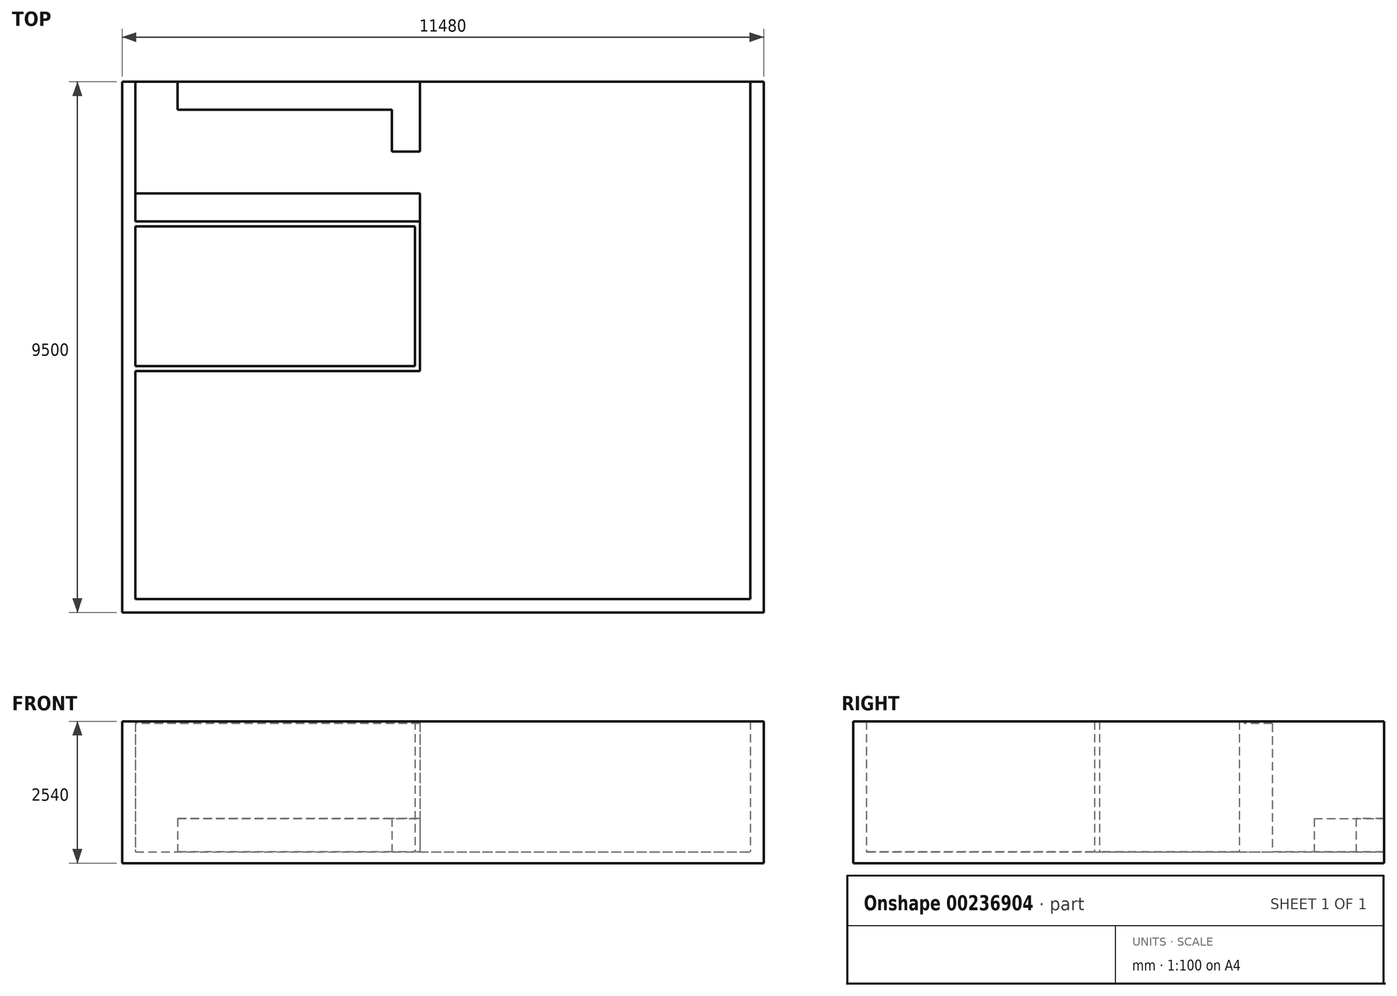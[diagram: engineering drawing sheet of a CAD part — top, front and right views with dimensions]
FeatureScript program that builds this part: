
annotation { "Feature Type Name" : "Feature", "Feature Type Description" : "" }
export const myFeature = defineFeature(function(context is Context, id is Id, definition is map)
    precondition{}
    {
        {
            var Q0;
            Q0=qCreatedBy(makeId("Top.planeOp"),FACE);
            var sketch = newSketch(context, id + "F0", { "sketchPlane" : qUnion([Q0])});
            skLineSegment(sketch, "E0.bottom", {"start": v(-5740, -4750) * mm, "end": v(5740, -4750) * mm});
            skLineSegment(sketch, "E0.top", {"start": v(-5740, 4750) * mm, "end": v(5740, 4750) * mm});
            skLineSegment(sketch, "E0.left", {"start": v(-5740, -4750) * mm, "end": v(-5740, 4750) * mm});
            skLineSegment(sketch, "E0.right", {"start": v(5740, -4750) * mm, "end": v(5740, 4750) * mm});
            skSolve(sketch);
        }
        {
            var Q0;
            Q0=makeQuery(id+"F0.imprint","IMPRINT",FACE,{"disambiguationData":[TD([[makeQuery(id+"F0.imprint","IMPRINT",EDGE,{"derivedFrom":sQuery(id+"F0.wireOp",EDGE,"E0.bottom")}),1.0]])]});
            extrude(context, id + "F1", {"entities" : qUnion([Q0]), "oppositeDirection" : true, "depth" : 200 * mm});
        }
        {
            var Q0;
            Q0=makeQuery(id+"F1.opExtrude","CAP_FACE",FACE,{"disambiguationData":[OSD([sQuery(id+"F0.wireOp",EDGE,"E0.bottom"),sQuery(id+"F0.wireOp",EDGE,"E0.top"),sQuery(id+"F0.wireOp",EDGE,"E0.left"),sQuery(id+"F0.wireOp",EDGE,"E0.right")])],"isStart":true});
            var sketch = newSketch(context, id + "F2", { "sketchPlane" : qUnion([Q0])});
            skLineSegment(sketch, "E1.bottom", {"start": v(-5740, 4750) * mm, "end": v(-5500, 4750) * mm});
            skLineSegment(sketch, "E1.top", {"start": v(-5740, -4750) * mm, "end": v(-5500, -4750) * mm});
            skLineSegment(sketch, "E1.left", {"start": v(-5740, 4750) * mm, "end": v(-5740, -4750) * mm});
            skLineSegment(sketch, "E1.right", {"start": v(-5500, 4750) * mm, "end": v(-5500, -4510) * mm});
            skLineSegment(sketch, "E2.bottom", {"start": v(-5500, -4750) * mm, "end": v(5740, -4750) * mm});
            skLineSegment(sketch, "E2.top", {"start": v(-5500, -4510) * mm, "end": v(5500, -4510) * mm});
            skLineSegment(sketch, "E2.right", {"start": v(5740, -4750) * mm, "end": v(5740, -4510) * mm});
            skLineSegment(sketch, "E3.top", {"start": v(5740, 4750) * mm, "end": v(5500, 4750) * mm});
            skLineSegment(sketch, "E3.left", {"start": v(5740, -4510) * mm, "end": v(5740, 4750) * mm});
            skLineSegment(sketch, "E3.right", {"start": v(5500, -4510) * mm, "end": v(5500, 4750) * mm});
            skSolve(sketch);
        }
        {
            var Q0;
            Q0=makeQuery(id+"F2.imprint","IMPRINT",FACE,{"disambiguationData":[TD([[makeQuery(id+"F2.imprint","IMPRINT",EDGE,{"derivedFrom":sQuery(id+"F2.wireOp",EDGE,"E1.bottom")}),-1.0]])]});
            extrude(context, id + "F3", {"entities" : qUnion([Q0]), "operationType" : NewBodyOperationType.ADD, "depth" : 2340 * mm});
        }
        {
            var Q0;
            Q0=makeQuery(id+"F1.opExtrude","CAP_FACE",FACE,{"disambiguationData":[OSD([sQuery(id+"F0.wireOp",EDGE,"E0.bottom"),sQuery(id+"F0.wireOp",EDGE,"E0.top"),sQuery(id+"F0.wireOp",EDGE,"E0.left"),sQuery(id+"F0.wireOp",EDGE,"E0.right")])],"isStart":true});
            var sketch = newSketch(context, id + "F4", { "sketchPlane" : qUnion([Q0])});
            skLineSegment(sketch, "E4.bottom", {"start": v(-5500, -430) * mm, "end": v(-410, -430) * mm});
            skLineSegment(sketch, "E4.top", {"start": v(-5500, -340) * mm, "end": v(-500, -340) * mm});
            skLineSegment(sketch, "E4.left", {"start": v(-5500, -430) * mm, "end": v(-5500, -340) * mm});
            skLineSegment(sketch, "E4.right", {"start": v(-410, -430) * mm, "end": v(-410, -340) * mm});
            skLineSegment(sketch, "E5.left", {"start": v(-410, 2160) * mm, "end": v(-410, 2160) * mm});
            skLineSegment(sketch, "E6.bottom", {"start": v(-500, 2160) * mm, "end": v(-5500, 2160) * mm});
            skLineSegment(sketch, "E6.top", {"start": v(-410, 2250) * mm, "end": v(-5500, 2250) * mm});
            skLineSegment(sketch, "E6.left", {"start": v(-410, 2160) * mm, "end": v(-410, 2250) * mm});
            skLineSegment(sketch, "E6.right", {"start": v(-5500, 2160) * mm, "end": v(-5500, 2250) * mm});
            skLineSegment(sketch, "E7.left", {"start": v(-410, -340) * mm, "end": v(-410, 2160) * mm});
            skLineSegment(sketch, "E7.right", {"start": v(-500, -340) * mm, "end": v(-500, 2160) * mm});
            skSolve(sketch);
        }
        {
            var Q0;
            Q0=makeQuery(id+"F4.imprint","IMPRINT",FACE,{"disambiguationData":[TD([[makeQuery(id+"F4.imprint","IMPRINT",EDGE,{"derivedFrom":sQuery(id+"F4.wireOp",EDGE,"E4.bottom")}),1.0]])]});
            extrude(context, id + "F5", {"entities" : qUnion([Q0]), "operationType" : NewBodyOperationType.ADD, "depth" : 2340 * mm});
        }
        {
            var Q0;
            {var subQ0=sQuery(id+"F0.wireOp",EDGE,"E0.top");Q0=makeQuery(id+"F5.boolean.opBoolean","SPLIT",FACE,{"disambiguationData":[TD([makeQuery(id+"F1.opExtrude","SWEPT_FACE",FACE,{"disambiguationData":[OSD([subQ0])]})])],"derivedFrom":makeQuery(id+"F1.opExtrude","CAP_FACE",FACE,{"disambiguationData":[OSD([sQuery(id+"F0.wireOp",EDGE,"E0.bottom"),subQ0,sQuery(id+"F0.wireOp",EDGE,"E0.left"),sQuery(id+"F0.wireOp",EDGE,"E0.right")])],"isStart":true})});}
            var sketch = newSketch(context, id + "F6", { "sketchPlane" : qUnion([Q0])});
            skLineSegment(sketch, "E8.bottom", {"start": v(-5500, 2250) * mm, "end": v(-410, 2250) * mm});
            skLineSegment(sketch, "E8.top", {"start": v(-5500, 2750) * mm, "end": v(-410, 2750) * mm});
            skLineSegment(sketch, "E8.left", {"start": v(-5500, 2250) * mm, "end": v(-5500, 2750) * mm});
            skLineSegment(sketch, "E8.right", {"start": v(-410, 2250) * mm, "end": v(-410, 2750) * mm});
            skLineSegment(sketch, "E9.bottom", {"start": v(-410, 3500) * mm, "end": v(-910, 3500) * mm});
            skLineSegment(sketch, "E9.top", {"start": v(-410, 4750) * mm, "end": v(-910, 4750) * mm});
            skLineSegment(sketch, "E9.left", {"start": v(-410, 3500) * mm, "end": v(-410, 4750) * mm});
            skLineSegment(sketch, "E9.right", {"start": v(-910, 3500) * mm, "end": v(-910, 4250) * mm});
            skLineSegment(sketch, "E10.bottom", {"start": v(-410, 4750) * mm, "end": v(-4750, 4750) * mm});
            skLineSegment(sketch, "E10.top", {"start": v(-910, 4250) * mm, "end": v(-4750, 4250) * mm});
            skLineSegment(sketch, "E10.left", {"start": v(-410, 4750) * mm, "end": v(-410, 4250) * mm});
            skLineSegment(sketch, "E10.right", {"start": v(-4750, 4750) * mm, "end": v(-4750, 4250) * mm});
            skSolve(sketch);
        }
        {
            var Q0;
            Q0=makeQuery(id+"F6.imprint","IMPRINT",FACE,{"disambiguationData":[TD([[makeQuery(id+"F6.imprint","IMPRINT",EDGE,{"derivedFrom":sQuery(id+"F6.wireOp",EDGE,"E8.bottom")}),-1.0]])]});
            extrude(context, id + "F7", {"entities" : qUnion([Q0]), "operationType" : NewBodyOperationType.ADD, "depth" : 2300 * mm});
        }
        {
            var Q0;
            Q0=makeQuery(id+"F6.imprint","IMPRINT",FACE,{"disambiguationData":[TD([[makeQuery(id+"F6.imprint","IMPRINT",EDGE,{"derivedFrom":sQuery(id+"F6.wireOp",EDGE,"E9.bottom")}),-1.0]])]});
            extrude(context, id + "F8", {"entities" : qUnion([Q0]), "operationType" : NewBodyOperationType.ADD, "depth" : 600 * mm});
        }
    });
